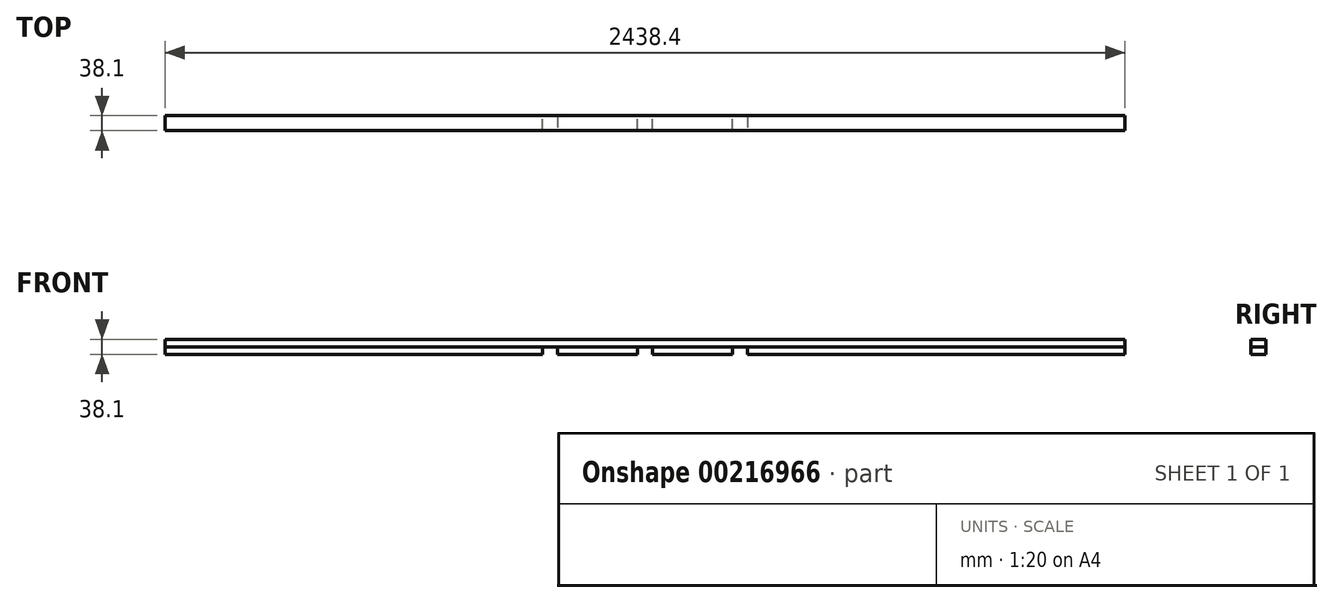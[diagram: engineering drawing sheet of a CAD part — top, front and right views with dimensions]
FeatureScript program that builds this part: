
annotation { "Feature Type Name" : "Feature", "Feature Type Description" : "" }
export const myFeature = defineFeature(function(context is Context, id is Id, definition is map)
    precondition{}
    {
        {
            var Q0;
            Q0=qCreatedBy(makeId("Top.planeOp"),FACE);
            var sketch = newSketch(context, id + "F0", { "sketchPlane" : qUnion([Q0])});
            skLineSegment(sketch, "E0", {"start": v(-1315.98, 0) * mm, "end": v(-1315.98, 38.1) * mm});
            skLineSegment(sketch, "E1", {"start": v(125.47, 0) * mm, "end": v(125.47, 38.1) * mm});
            skLineSegment(sketch, "E2", {"start": v(-77.73, 0) * mm, "end": v(-77.73, 38.1) * mm});
            skLineSegment(sketch, "E3", {"start": v(-1315.98, 38.1) * mm, "end": v(-1315.98, 0) * mm});
            skLineSegment(sketch, "E4", {"start": v(-115.83, 0) * mm, "end": v(-115.83, 38.1) * mm});
            skLineSegment(sketch, "E5", {"start": v(-115.83, 38.1) * mm, "end": v(-319.03, 38.1) * mm});
            skLineSegment(sketch, "E6", {"start": v(-319.03, 38.1) * mm, "end": v(-319.03, 0) * mm});
            skLineSegment(sketch, "E7", {"start": v(-357.13, 0) * mm, "end": v(-357.13, 38.1) * mm});
            skLineSegment(sketch, "E8", {"start": v(-357.13, 38.1) * mm, "end": v(-1315.98, 38.1) * mm});
            skLineSegment(sketch, "E9.trimOffspring", {"start": v(-1315.98, 38.1) * mm, "end": v(-357.13, 38.1) * mm});
            skLineSegment(sketch, "E10.trimOffspring", {"start": v(-319.03, 38.1) * mm, "end": v(-115.83, 38.1) * mm});
            skLineSegment(sketch, "E11.trimOffspring", {"start": v(-357.13, 0) * mm, "end": v(-1315.98, 0) * mm});
            skLineSegment(sketch, "E12.trimOffspring", {"start": v(-115.83, 0) * mm, "end": v(-319.03, 0) * mm});
            skLineSegment(sketch, "E13.trimOffspring", {"start": v(-77.73, 38.1) * mm, "end": v(125.47, 38.1) * mm});
            skPoint(sketch, "E14", {"position": v(-1315.98, 0) * mm});
            skLineSegment(sketch, "E15", {"start": v(-77.73, 0) * mm, "end": v(125.47, 0) * mm});
            skLineSegment(sketch, "E16.bottom", {"start": v(163.57, 38.1) * mm, "end": v(1122.42, 38.1) * mm});
            skLineSegment(sketch, "E16.top", {"start": v(163.57, 0) * mm, "end": v(1122.42, 0) * mm});
            skLineSegment(sketch, "E16.left", {"start": v(163.57, 38.1) * mm, "end": v(163.57, 0) * mm});
            skLineSegment(sketch, "E16.right", {"start": v(1122.42, 38.1) * mm, "end": v(1122.42, 0) * mm});
            skSolve(sketch);
        }
        {
            var Q0;
            Q0=qSketchRegion(id+"F0",true);
            extrude(context, id + "F1", {"entities" : qUnion([Q0]), "depth" : 19.05 * mm, "offsetDistance" : 25.4 * mm});
        }
        {
            var Q0;
            Q0=makeQuery(id+"F1.opExtrude","CAP_FACE",FACE,{"disambiguationData":[OSD([sQuery(id+"F0.wireOp",EDGE,"E7"),sQuery(id+"F0.wireOp",EDGE,"E3"),sQuery(id+"F0.wireOp",EDGE,"E9.trimOffspring"),sQuery(id+"F0.wireOp",EDGE,"E11.trimOffspring")])],"isStart":false});
            var sketch = newSketch(context, id + "F2", { "sketchPlane" : qUnion([Q0])});
            skLineSegment(sketch, "E17.bottom", {"start": v(-1315.98, 38.1) * mm, "end": v(1122.42, 38.1) * mm});
            skLineSegment(sketch, "E17.top", {"start": v(-1315.98, 0) * mm, "end": v(1122.42, 0) * mm});
            skLineSegment(sketch, "E17.left", {"start": v(-1315.98, 38.1) * mm, "end": v(-1315.98, 0) * mm});
            skLineSegment(sketch, "E17.right", {"start": v(1122.42, 38.1) * mm, "end": v(1122.42, 0) * mm});
            skSolve(sketch);
        }
        {
            var Q0;
            Q0 = qSketchRegion(id + "F2", true);
            extrude(context, id + "F3", {"entities" : qUnion([Q0]), "depth" : 19.05 * mm});
        }
    });
